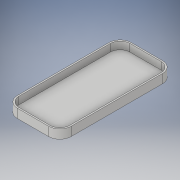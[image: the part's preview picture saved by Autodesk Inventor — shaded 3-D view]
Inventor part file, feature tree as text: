
AUTODESK INVENTOR PART (.ipt)
format: ipt  version: 2018 (Build 220112000, 112)  size: 330,240 bytes
history: native  units: mm
features: extrude x2, other x2, sketch x2, projected_geometry x1
ambient origin geometry x8: Origin, YZ Plane, XZ Plane, XY Plane, X Axis, Y Axis, Z Axis, Center Point
bodies: Volumenkörper1 (feature_tree)
feature tree (7):
  extrude  "Extrusion1"  Depth=153.0mm
  extrude  "Extrusion2"  TaperAngle=0.0deg  [1 undecoded]
  other  "Prägen1"
  sketch  "Skizze1"  dims[d0=72.0mm d1=153.0mm]
  sketch  "Skizze2"  dims[d2=12.0mm d3=0.0mm d4=15.0mm d5=15.0mm d6=149.0mm d7=68.0mm d8=13.0mm d9=10.0mm d10=0.0mm d11=76.5mm d12=1.0mm d13=0.0mm]
  other  "TextSkizze"
  projected_geometry  "Projizierte Kontur1"
note: 1 required parameter value undecoded (feature->parameter linkage not recoverable at this tier; creation-order binding heuristic only, values carry confidence <= 0.55)
